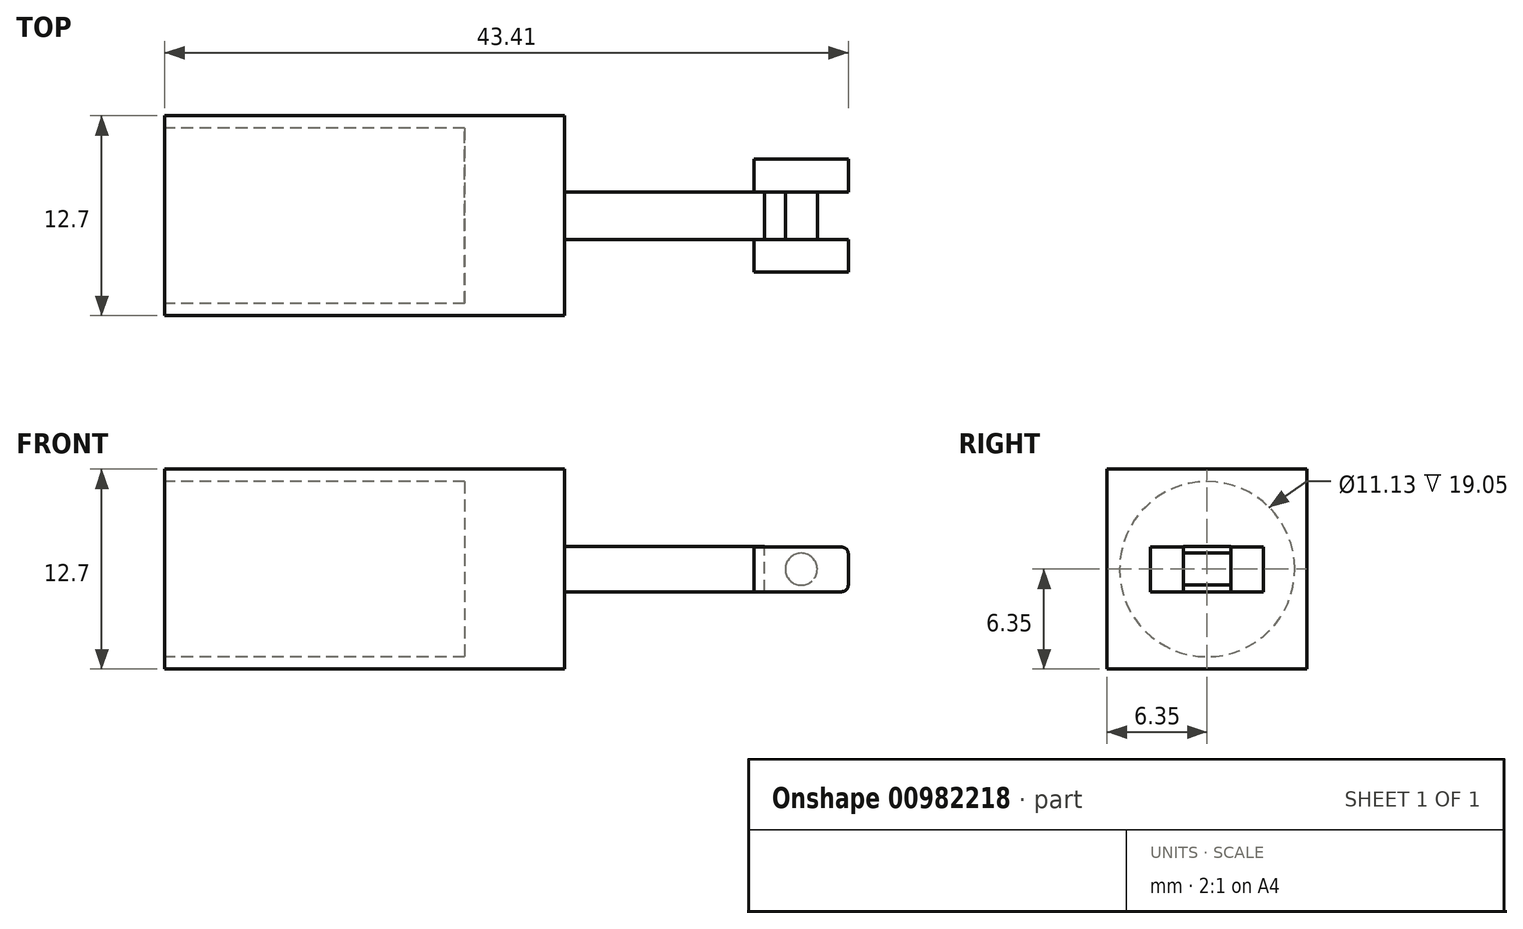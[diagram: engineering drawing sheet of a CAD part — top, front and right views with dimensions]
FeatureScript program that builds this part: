
annotation { "Feature Type Name" : "Feature", "Feature Type Description" : "" }
export const myFeature = defineFeature(function(context is Context, id is Id, definition is map)
    precondition{}
    {
        {
            var Q0;
            Q0=qCreatedBy(makeId("Right.planeOp"),FACE);
            var sketch = newSketch(context, id + "F0", { "sketchPlane" : qUnion([Q0])});
            skLineSegment(sketch, "E0.bottom", {"start": v(6.35, -6.35) * mm, "end": v(-6.35, -6.35) * mm});
            skLineSegment(sketch, "E0.top", {"start": v(6.35, 6.35) * mm, "end": v(-6.35, 6.35) * mm});
            skLineSegment(sketch, "E0.left", {"start": v(6.35, -6.35) * mm, "end": v(6.35, 6.35) * mm});
            skLineSegment(sketch, "E0.right", {"start": v(-6.35, -6.35) * mm, "end": v(-6.35, 6.35) * mm});
            skPoint(sketch, "E0.middle", {"position": v(0, 0) * mm});
            skSolve(sketch);
        }
        {
            var Q0;
            Q0=makeQuery(id+"F0.imprint","IMPRINT",FACE,{"disambiguationData":[TD([[makeQuery(id+"F0.imprint","IMPRINT",EDGE,{"derivedFrom":sQuery(id+"F0.wireOp",EDGE,"E0.bottom")}),-1.0]])]});
            extrude(context, id + "F1", {"entities" : qUnion([Q0]), "oppositeDirection" : true, "depth" : 25.4 * mm, "offsetDistance" : 25.4 * mm});
        }
        {
            var Q0;
            Q0=makeQuery(id+"F1.opExtrude","CAP_FACE",FACE,{"disambiguationData":[OSD([sQuery(id+"F0.wireOp",EDGE,"E0.bottom"),sQuery(id+"F0.wireOp",EDGE,"E0.top"),sQuery(id+"F0.wireOp",EDGE,"E0.left"),sQuery(id+"F0.wireOp",EDGE,"E0.right")])],"isStart":false});
            var sketch = newSketch(context, id + "F2", { "sketchPlane" : qUnion([Q0])});
            skCircle(sketch, "E1", {"center": v(0, 0) * mm, "radius": 5.56 * mm});
            skSolve(sketch);
        }
        {
            var Q0;
            Q0=makeQuery(id+"F2.imprint","IMPRINT",FACE,{"disambiguationData":[TD([[makeQuery(id+"F2.imprint","IMPRINT",EDGE,{"derivedFrom":sQuery(id+"F2.wireOp",EDGE,"E1")}),1.0]])]});
            extrude(context, id + "F3", {"entities" : qUnion([Q0]), "operationType" : NewBodyOperationType.REMOVE, "oppositeDirection" : true, "depth" : 19.05 * mm, "offsetDistance" : 25.4 * mm});
        }
        {
            var Q0;
            Q0=makeQuery(id+"F1.opExtrude","CAP_FACE",FACE,{"disambiguationData":[OSD([sQuery(id+"F0.wireOp",EDGE,"E0.bottom"),sQuery(id+"F0.wireOp",EDGE,"E0.top"),sQuery(id+"F0.wireOp",EDGE,"E0.left"),sQuery(id+"F0.wireOp",EDGE,"E0.right")])],"isStart":true});
            var sketch = newSketch(context, id + "F4", { "sketchPlane" : qUnion([Q0])});
            skLineSegment(sketch, "E2.bottom", {"start": v(1.51, -1.44) * mm, "end": v(-1.51, -1.44) * mm});
            skLineSegment(sketch, "E2.top", {"start": v(1.51, 1.44) * mm, "end": v(-1.51, 1.44) * mm});
            skLineSegment(sketch, "E2.left", {"start": v(1.51, -1.44) * mm, "end": v(1.51, 1.44) * mm});
            skLineSegment(sketch, "E2.right", {"start": v(-1.51, -1.44) * mm, "end": v(-1.51, 1.44) * mm});
            skPoint(sketch, "E2.middle", {"position": v(0, 0) * mm});
            skSolve(sketch);
        }
        {
            var Q0;
            Q0=makeQuery(id+"F4.imprint","IMPRINT",FACE,{"disambiguationData":[TD([[makeQuery(id+"F4.imprint","IMPRINT",EDGE,{"derivedFrom":sQuery(id+"F4.wireOp",EDGE,"E2.bottom")}),-1.0]])]});
            extrude(context, id + "F5", {"entities" : qUnion([Q0]), "operationType" : NewBodyOperationType.ADD, "depth" : 12.7 * mm, "offsetDistance" : 25.4 * mm});
        }
        {
            var Q0;
            Q0=makeQuery(id+"F5.opExtrude","SWEPT_FACE",FACE,{"disambiguationData":[OSD([sQuery(id+"F4.wireOp",EDGE,"E2.bottom")])]});
            var sketch = newSketch(context, id + "F6", { "sketchPlane" : qUnion([Q0])});
            skLineSegment(sketch, "E3.bottom", {"start": v(12.03, 1.51) * mm, "end": v(18.01, 1.51) * mm});
            skLineSegment(sketch, "E3.top", {"start": v(12.03, 3.59) * mm, "end": v(18.01, 3.59) * mm});
            skLineSegment(sketch, "E3.left", {"start": v(12.03, 1.51) * mm, "end": v(12.03, 3.59) * mm});
            skLineSegment(sketch, "E3.right", {"start": v(18.01, 1.51) * mm, "end": v(18.01, 3.59) * mm});
            skLineSegment(sketch, "E4", {"start": v(12.7, 0) * mm, "end": v(17.95, 0) * mm, "construction": true});
            skLineSegment(sketch, "E5.MirrorCS", {"start": v(12.03, -1.51) * mm, "end": v(18.01, -1.51) * mm});
            skLineSegment(sketch, "E6.MirrorCS", {"start": v(18.01, -1.51) * mm, "end": v(18.01, -3.59) * mm});
            skLineSegment(sketch, "E7.MirrorCS", {"start": v(12.03, -3.59) * mm, "end": v(18.01, -3.59) * mm});
            skLineSegment(sketch, "E8.MirrorCS", {"start": v(12.03, -1.51) * mm, "end": v(12.03, -3.59) * mm});
            skSolve(sketch);
        }
        {
            var Q0;
            Q0=makeQuery(id+"F6.imprint","IMPRINT",FACE,{"disambiguationData":[TD([[makeQuery(id+"F6.imprint","IMPRINT",EDGE,{"derivedFrom":sQuery(id+"F6.wireOp",EDGE,"E3.top")}),-1.0]])]});
            var Q1;
            {var subQ0=sQuery(id+"F6.wireOp",EDGE,"E6.MirrorCS");Q1=makeQuery(id+"F6.imprint","IMPRINT",FACE,{"disambiguationData":[TD([[makeQuery(id+"F6.imprint","IMPRINT",EDGE,{"derivedFrom":subQ0}),-1.0]])]});}
            extrude(context, id + "F7", {"entities" : qUnion([Q0, Q1]), "operationType" : NewBodyOperationType.ADD, "oppositeDirection" : true, "depth" : 2.84 * mm, "offsetDistance" : 25.4 * mm});
        }
        {
            var Q0;
            Q0=makeQuery(id+"F7.opExtrude","SWEPT_FACE",FACE,{"disambiguationData":[OSD([sQuery(id+"F6.wireOp",EDGE,"E3.top")])]});
            var sketch = newSketch(context, id + "F8", { "sketchPlane" : qUnion([Q0])});
            skLineSegment(sketch, "E9", {"start": v(18.01, 1.4) * mm, "end": v(12.03, -1.44) * mm, "construction": true});
            skLineSegment(sketch, "E10", {"start": v(12.03, 1.4) * mm, "end": v(18.01, -1.44) * mm, "construction": true});
            skPoint(sketch, "E11", {"position": v(15.02, 0) * mm});
            skPoint(sketch, "E11.positionSnap0", {"position": v(15.02, -0.01) * mm});
            skCircle(sketch, "E12", {"center": v(15.02, 0) * mm, "radius": 1.02 * mm});
            skSolve(sketch);
        }
        {
            var Q0;
            Q0=makeQuery(id+"F8.imprint","IMPRINT",FACE,{"disambiguationData":[TD([[makeQuery(id+"F8.imprint","IMPRINT",EDGE,{"derivedFrom":sQuery(id+"F8.wireOp",EDGE,"E12")}),1.0]])]});
            extrude(context, id + "F9", {"entities" : qUnion([Q0]), "operationType" : NewBodyOperationType.ADD, "oppositeDirection" : true, "depth" : 5.28 * mm, "offsetDistance" : 25.4 * mm});
        }
        {
            var Q0;
            Q0=makeQuery(id+"F7.opExtrude","CAP_EDGE",EDGE,{"disambiguationData":[OSD([sQuery(id+"F6.wireOp",EDGE,"E3.right")])],"isStart":true});
            var Q1;
            Q1=makeQuery(id+"F7.opExtrude","CAP_EDGE",EDGE,{"disambiguationData":[OSD([sQuery(id+"F6.wireOp",EDGE,"E6.MirrorCS")])],"isStart":true});
            var Q2;
            Q2=makeQuery(id+"F7.opExtrude","CAP_EDGE",EDGE,{"disambiguationData":[OSD([sQuery(id+"F6.wireOp",EDGE,"E6.MirrorCS")])],"isStart":false});
            var Q3;
            Q3=makeQuery(id+"F7.opExtrude","CAP_EDGE",EDGE,{"disambiguationData":[OSD([sQuery(id+"F6.wireOp",EDGE,"E3.right")])],"isStart":false});
            fillet(context, id + "F10", {"entities" : qUnion([Q0, Q1, Q2, Q3]), "radius" : 0.5 * mm, "tangentPropagation" : true, "rho" : 0.5, "crossSection" : FilletCrossSection.CONIC, "allowEdgeOverflow" : false});
        }
    });
